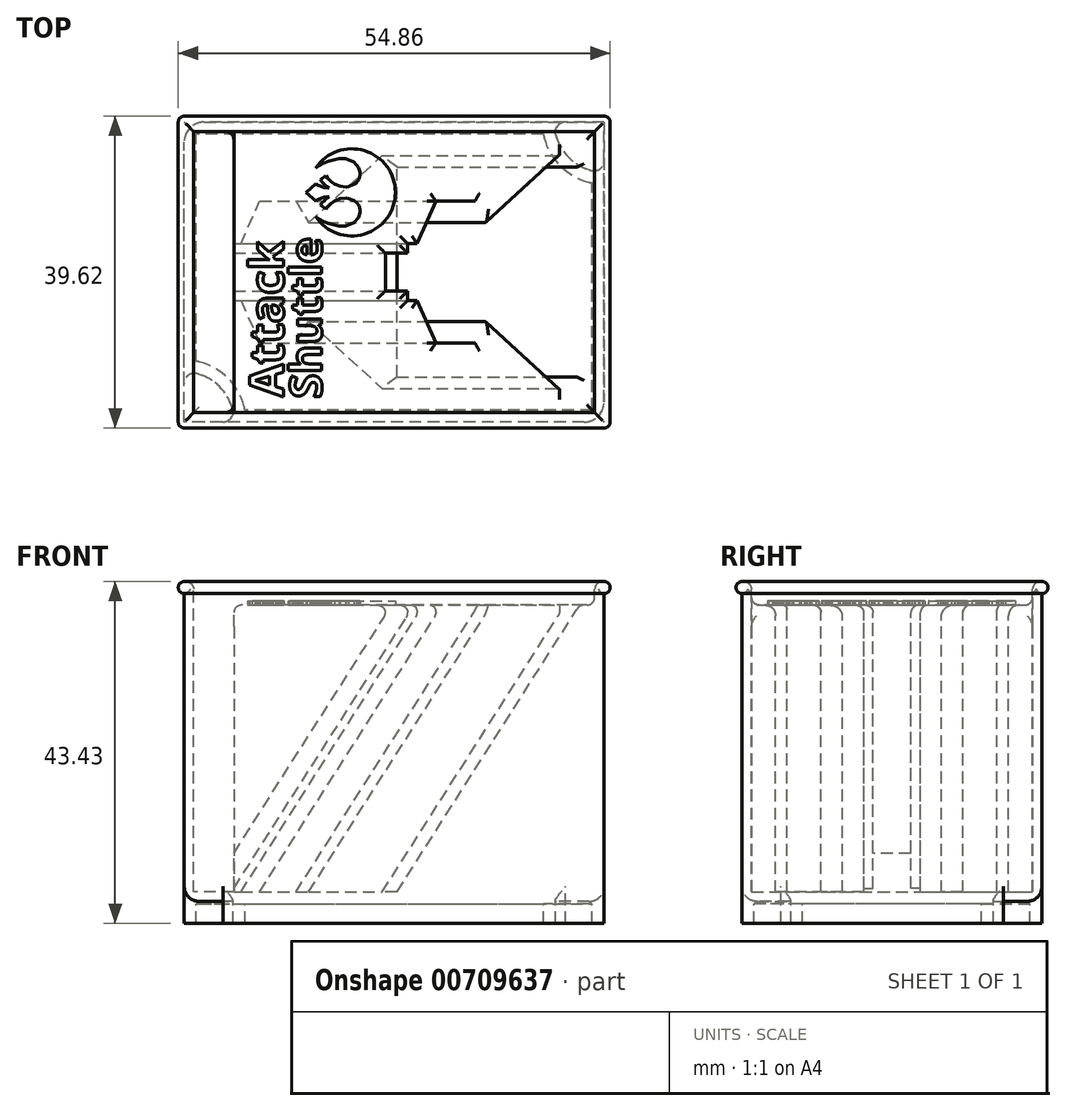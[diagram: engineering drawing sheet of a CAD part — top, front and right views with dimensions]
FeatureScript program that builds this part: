
annotation { "Feature Type Name" : "Feature", "Feature Type Description" : "" }
export const myFeature = defineFeature(function(context is Context, id is Id, definition is map)
    precondition{}
    {
        {
            var Q0;
            Q0=qCreatedBy(makeId("Front.planeOp"),FACE);
            var sketch = newSketch(context, id + "F0", { "sketchPlane" : qUnion([Q0])});
            skLineSegment(sketch, "E0.bottom", {"start": v(26.67, -20.32) * mm, "end": v(-26.67, -20.32) * mm});
            skLineSegment(sketch, "E0.top", {"start": v(26.67, 20.32) * mm, "end": v(-26.67, 20.32) * mm});
            skLineSegment(sketch, "E0.left", {"start": v(26.67, -20.32) * mm, "end": v(26.67, 20.32) * mm});
            skLineSegment(sketch, "E0.right", {"start": v(-26.67, -20.32) * mm, "end": v(-26.67, 20.32) * mm});
            skPoint(sketch, "E0.middle", {"position": v(0, 0) * mm});
            skSolve(sketch);
        }
        {
            var Q0;
            Q0=makeQuery(id+"F0.imprint","IMPRINT",FACE,{"disambiguationData":[TD([[makeQuery(id+"F0.imprint","IMPRINT",EDGE,{"derivedFrom":sQuery(id+"F0.wireOp",EDGE,"E0.bottom")}),-1.0]])]});
            extrude(context, id + "F1", {"entities" : qUnion([Q0]), "depth" : 38.1 * mm, "symmetric" : true});
        }
        {
            var Q0;
            Q0=makeQuery(id+"F1.opExtrude","SWEPT_FACE",FACE,{"disambiguationData":[OSD([sQuery(id+"F0.wireOp",EDGE,"E0.top")])]});
            shell(context, id + "F2", {"entities" : qUnion([Q0]), "thickness" : 1.2 * mm});
        }
        {
            var Q0;
            Q0=makeQuery(id+"F1.opExtrude","CAP_FACE",FACE,{"disambiguationData":[OSD([sQuery(id+"F0.wireOp",EDGE,"E0.bottom"),sQuery(id+"F0.wireOp",EDGE,"E0.top"),sQuery(id+"F0.wireOp",EDGE,"E0.left"),sQuery(id+"F0.wireOp",EDGE,"E0.right")])],"isStart":false});
            var sketch = newSketch(context, id + "F3", { "sketchPlane" : qUnion([Q0])});
            skArc(sketch, "E1", {"start": v(-26.67, 20.32) * mm, "mid": v(-27.43, 19.56) * mm, "end": v(-26.67, 18.8) * mm});
            skSolve(sketch);
        }
        {
            var Q0;
            {var subQ0=sQuery(id+"F3.wireOp",EDGE,"E1");Q0=makeQuery(id+"F3.imprint","IMPRINT",FACE,{"disambiguationData":[TD([[makeQuery(id+"F3.imprint","IMPRINT",EDGE,{"derivedFrom":subQ0}),1.0]])]});}
            var Q1;
            Q1=makeQuery(id+"F1.opExtrude","SWEPT_EDGE",EDGE,{"disambiguationData":[OSD([sQuery(id+"F0.wireOp",EDGE,"E0.top"),sQuery(id+"F0.wireOp",EDGE,"E0.right")])]});
            var Q2;
            Q2=makeQuery(id+"F1.opExtrude","CAP_EDGE",EDGE,{"disambiguationData":[OSD([sQuery(id+"F0.wireOp",EDGE,"E0.top")])],"isStart":true});
            var Q3;
            Q3=makeQuery(id+"F1.opExtrude","SWEPT_EDGE",EDGE,{"disambiguationData":[OSD([sQuery(id+"F0.wireOp",EDGE,"E0.top"),sQuery(id+"F0.wireOp",EDGE,"E0.left")])]});
            var Q4;
            Q4=makeQuery(id+"F1.opExtrude","CAP_EDGE",EDGE,{"disambiguationData":[OSD([sQuery(id+"F0.wireOp",EDGE,"E0.top")])],"isStart":false});
            sweep(context, id + "F4", {"operationType" : NewBodyOperationType.ADD, "profiles" : qUnion([Q0]), "path" : qUnion([Q1, Q2, Q3, Q4])});
        }
        {
            var Q0;
            Q0=makeQuery(id+"F1.opExtrude","SWEPT_FACE",FACE,{"disambiguationData":[OSD([sQuery(id+"F0.wireOp",EDGE,"E0.bottom")])]});
            var sketch = newSketch(context, id + "F5", { "sketchPlane" : qUnion([Q0])});
            skLineSegment(sketch, "E2.bottom", {"start": v(26.67, 19.05) * mm, "end": v(21.75, 19.05) * mm});
            skLineSegment(sketch, "E2.left", {"start": v(26.67, 19.05) * mm, "end": v(26.67, 14.13) * mm});
            skPoint(sketch, "E3.newPointA", {"position": v(20.32, 19.05) * mm});
            skArc(sketch, "E4", {"start": v(20.52, 17.46) * mm, "mid": v(22.18, 14.56) * mm, "end": v(25.08, 12.9) * mm});
            skArc(sketch, "E5.filletArc", {"start": v(21.75, 19.05) * mm, "mid": v(20.75, 18.56) * mm, "end": v(20.52, 17.46) * mm});
            skPoint(sketch, "E6.visualSharp", {"position": v(26.67, 12.7) * mm});
            skArc(sketch, "E6.filletArc", {"start": v(25.08, 12.9) * mm, "mid": v(26.18, 13.13) * mm, "end": v(26.67, 14.13) * mm});
            skArc(sketch, "E7.MirrorCS", {"start": v(-21.75, 19.05) * mm, "mid": v(-20.75, 18.56) * mm, "end": v(-20.52, 17.46) * mm});
            skArc(sketch, "E8.MirrorCS", {"start": v(-20.52, 17.46) * mm, "mid": v(-22.18, 14.56) * mm, "end": v(-25.08, 12.9) * mm});
            skArc(sketch, "E9.MirrorCS", {"start": v(-25.08, 12.9) * mm, "mid": v(-26.18, 13.13) * mm, "end": v(-26.67, 14.13) * mm});
            skLineSegment(sketch, "E10.MirrorCS", {"start": v(-26.67, 19.05) * mm, "end": v(-26.67, 14.13) * mm});
            skLineSegment(sketch, "E11.MirrorCS", {"start": v(-26.67, 19.05) * mm, "end": v(-21.75, 19.05) * mm});
            skArc(sketch, "E12.MirrorCS", {"start": v(-20.52, -17.46) * mm, "mid": v(-22.18, -14.56) * mm, "end": v(-25.08, -12.9) * mm});
            skArc(sketch, "E13.MirrorCS", {"start": v(-21.75, -19.05) * mm, "mid": v(-20.75, -18.56) * mm, "end": v(-20.52, -17.46) * mm});
            skLineSegment(sketch, "E14.MirrorCS", {"start": v(-26.67, -19.05) * mm, "end": v(-21.75, -19.05) * mm});
            skLineSegment(sketch, "E15.MirrorCS", {"start": v(-26.67, -19.05) * mm, "end": v(-26.67, -14.13) * mm});
            skArc(sketch, "E16.MirrorCS", {"start": v(-25.08, -12.9) * mm, "mid": v(-26.18, -13.13) * mm, "end": v(-26.67, -14.13) * mm});
            skArc(sketch, "E17.MirrorCS", {"start": v(21.75, -19.05) * mm, "mid": v(20.75, -18.56) * mm, "end": v(20.52, -17.46) * mm});
            skArc(sketch, "E18.MirrorCS", {"start": v(20.52, -17.46) * mm, "mid": v(22.18, -14.56) * mm, "end": v(25.08, -12.9) * mm});
            skArc(sketch, "E19.MirrorCS", {"start": v(25.08, -12.9) * mm, "mid": v(26.18, -13.13) * mm, "end": v(26.67, -14.13) * mm});
            skLineSegment(sketch, "E20.MirrorCS", {"start": v(26.67, -19.05) * mm, "end": v(26.67, -14.13) * mm});
            skLineSegment(sketch, "E21.MirrorCS", {"start": v(26.67, -19.05) * mm, "end": v(21.75, -19.05) * mm});
            skSolve(sketch);
        }
        {
            var Q0;
            Q0=makeQuery(id+"F5.imprint","IMPRINT",FACE,{"disambiguationData":[TD([[makeQuery(id+"F5.imprint","IMPRINT",EDGE,{"derivedFrom":sQuery(id+"F5.wireOp",EDGE,"E2.bottom")}),1.0]])]});
            var Q1;
            Q1=makeQuery(id+"F5.imprint","IMPRINT",FACE,{"disambiguationData":[TD([[makeQuery(id+"F5.imprint","IMPRINT",EDGE,{"derivedFrom":sQuery(id+"F5.wireOp",EDGE,"E8.MirrorCS")}),-1.0]])]});
            var Q2;
            Q2=makeQuery(id+"F5.imprint","IMPRINT",FACE,{"disambiguationData":[TD([[makeQuery(id+"F5.imprint","IMPRINT",EDGE,{"derivedFrom":sQuery(id+"F5.wireOp",EDGE,"E12.MirrorCS")}),1.0]])]});
            var Q3;
            Q3=makeQuery(id+"F5.imprint","IMPRINT",FACE,{"disambiguationData":[TD([[makeQuery(id+"F5.imprint","IMPRINT",EDGE,{"derivedFrom":sQuery(id+"F5.wireOp",EDGE,"E17.MirrorCS")}),-1.0]])]});
            extrude(context, id + "F6", {"entities" : qUnion([Q0, Q1, Q2, Q3]), "operationType" : NewBodyOperationType.ADD, "depth" : 2.8 * mm});
        }
        {
            var Q0;
            Q0=makeQuery(id+"F6.opExtrude","CAP_FACE",FACE,{"disambiguationData":[OSD([sQuery(id+"F5.wireOp",EDGE,"E2.bottom"),sQuery(id+"F5.wireOp",EDGE,"E2.left"),sQuery(id+"F5.wireOp",EDGE,"E4"),sQuery(id+"F5.wireOp",EDGE,"E5.filletArc"),sQuery(id+"F5.wireOp",EDGE,"E6.filletArc")])],"isStart":false});
            var Q1;
            Q1=makeQuery(id+"F6.opExtrude","CAP_FACE",FACE,{"disambiguationData":[OSD([sQuery(id+"F5.wireOp",EDGE,"E8.MirrorCS"),sQuery(id+"F5.wireOp",EDGE,"E9.MirrorCS"),sQuery(id+"F5.wireOp",EDGE,"E10.MirrorCS"),sQuery(id+"F5.wireOp",EDGE,"E7.MirrorCS"),sQuery(id+"F5.wireOp",EDGE,"E11.MirrorCS")])],"isStart":false});
            var Q2;
            Q2=makeQuery(id+"F6.opExtrude","CAP_FACE",FACE,{"disambiguationData":[OSD([sQuery(id+"F5.wireOp",EDGE,"E12.MirrorCS"),sQuery(id+"F5.wireOp",EDGE,"E13.MirrorCS"),sQuery(id+"F5.wireOp",EDGE,"E14.MirrorCS"),sQuery(id+"F5.wireOp",EDGE,"E15.MirrorCS"),sQuery(id+"F5.wireOp",EDGE,"E16.MirrorCS")])],"isStart":false});
            var Q3;
            Q3=makeQuery(id+"F6.opExtrude","CAP_FACE",FACE,{"disambiguationData":[OSD([sQuery(id+"F5.wireOp",EDGE,"E17.MirrorCS"),sQuery(id+"F5.wireOp",EDGE,"E18.MirrorCS"),sQuery(id+"F5.wireOp",EDGE,"E19.MirrorCS"),sQuery(id+"F5.wireOp",EDGE,"E20.MirrorCS"),sQuery(id+"F5.wireOp",EDGE,"E21.MirrorCS")])],"isStart":false});
            shell(context, id + "F7", {"entities" : qUnion([Q0, Q1, Q2, Q3]), "thickness" : 1.52 * mm});
        }
        {
            var Q0;
            Q0=makeQuery(id+"F1.opExtrude","SWEPT_EDGE",EDGE,{"disambiguationData":[OSD([sQuery(id+"F0.wireOp",EDGE,"E0.bottom"),sQuery(id+"F0.wireOp",EDGE,"E0.right")])]});
            var Q1;
            Q1=makeQuery(id+"F1.opExtrude","CAP_EDGE",EDGE,{"disambiguationData":[OSD([sQuery(id+"F0.wireOp",EDGE,"E0.bottom")])],"isStart":false});
            var Q2;
            Q2=makeQuery(id+"F1.opExtrude","SWEPT_EDGE",EDGE,{"disambiguationData":[OSD([sQuery(id+"F0.wireOp",EDGE,"E0.bottom"),sQuery(id+"F0.wireOp",EDGE,"E0.left")])]});
            var Q3;
            Q3=makeQuery(id+"F1.opExtrude","CAP_EDGE",EDGE,{"disambiguationData":[OSD([sQuery(id+"F0.wireOp",EDGE,"E0.bottom")])],"isStart":true});
            fillet(context, id + "F8", {"entities" : qUnion([Q0, Q1, Q2, Q3]), "radius" : 1.9 * mm, "tangentPropagation" : true, "allowEdgeOverflow" : false});
        }
        {
            var Q0;
            Q0=makeQuery(id+"F4.opSweep","MID_CAP_EDGE",EDGE,{"disambiguationData":[OSD([sQuery(id+"F0.wireOp",EDGE,"E0.top"),sQuery(id+"F0.wireOp",EDGE,"E0.left"),sQuery(id+"F3.wireOp",EDGE,"E1")])],"capPos":3.0});
            var Q1;
            Q1=makeQuery(id+"F4.opSweep","MID_CAP_EDGE",EDGE,{"disambiguationData":[OSD([sQuery(id+"F0.wireOp",EDGE,"E0.top"),sQuery(id+"F0.wireOp",EDGE,"E0.left"),sQuery(id+"F3.wireOp",EDGE,"E1")])],"capPos":2.0});
            var Q2;
            Q2=makeQuery(id+"F4.opSweep","MID_CAP_EDGE",EDGE,{"disambiguationData":[OSD([sQuery(id+"F0.wireOp",EDGE,"E0.top"),sQuery(id+"F0.wireOp",EDGE,"E0.right"),sQuery(id+"F3.wireOp",EDGE,"E1")])],"capPos":1.0});
            var Q3;
            Q3=makeQuery(id+"F4.opSweep","CAP_EDGE",EDGE,{"disambiguationData":[OSD([sQuery(id+"F0.wireOp",EDGE,"E0.top"),sQuery(id+"F0.wireOp",EDGE,"E0.right"),sQuery(id+"F3.wireOp",EDGE,"E1")])],"isStart":true});
            fillet(context, id + "F9", {"entities" : qUnion([Q0, Q1, Q2, Q3]), "radius" : 0.76 * mm, "tangentPropagation" : true, "allowEdgeOverflow" : false});
        }
        {
            var Q0;
            Q0=makeQuery(id+"F6.boolean.opBoolean","MERGE",EDGE,{"derivedFrom":[makeQuery(id+"F1.opExtrude","CAP_EDGE",EDGE,{"disambiguationData":[OSD([sQuery(id+"F0.wireOp",EDGE,"E0.left")])],"isStart":false}),makeQuery(id+"F6.opExtrude","SWEPT_EDGE",EDGE,{"disambiguationData":[OSD([sQuery(id+"F5.wireOp",EDGE,"E2.bottom"),sQuery(id+"F5.wireOp",EDGE,"E2.left")])]})]});
            var Q1;
            Q1=makeQuery(id+"F6.boolean.opBoolean","MERGE",EDGE,{"derivedFrom":[makeQuery(id+"F1.opExtrude","CAP_EDGE",EDGE,{"disambiguationData":[OSD([sQuery(id+"F0.wireOp",EDGE,"E0.left")])],"isStart":true}),makeQuery(id+"F6.opExtrude","SWEPT_EDGE",EDGE,{"disambiguationData":[OSD([sQuery(id+"F5.wireOp",EDGE,"E20.MirrorCS"),sQuery(id+"F5.wireOp",EDGE,"E21.MirrorCS")])]})]});
            var Q2;
            Q2=makeQuery(id+"F6.boolean.opBoolean","MERGE",EDGE,{"derivedFrom":[makeQuery(id+"F1.opExtrude","CAP_EDGE",EDGE,{"disambiguationData":[OSD([sQuery(id+"F0.wireOp",EDGE,"E0.right")])],"isStart":false}),makeQuery(id+"F6.opExtrude","SWEPT_EDGE",EDGE,{"disambiguationData":[OSD([sQuery(id+"F5.wireOp",EDGE,"E10.MirrorCS"),sQuery(id+"F5.wireOp",EDGE,"E11.MirrorCS")])]})]});
            var Q3;
            Q3=makeQuery(id+"F6.boolean.opBoolean","MERGE",EDGE,{"derivedFrom":[makeQuery(id+"F1.opExtrude","CAP_EDGE",EDGE,{"disambiguationData":[OSD([sQuery(id+"F0.wireOp",EDGE,"E0.right")])],"isStart":true}),makeQuery(id+"F6.opExtrude","SWEPT_EDGE",EDGE,{"disambiguationData":[OSD([sQuery(id+"F5.wireOp",EDGE,"E14.MirrorCS"),sQuery(id+"F5.wireOp",EDGE,"E15.MirrorCS")])]})]});
            fillet(context, id + "F10", {"entities" : qUnion([Q0, Q1, Q2, Q3]), "radius" : 2.54 * mm, "tangentPropagation" : true, "allowEdgeOverflow" : false});
        }
        {
            var Q0;
            Q0=makeQuery(id+"F2.opShell","OFFSET_EDGE",EDGE,{"disambiguationData":[OSD([sQuery(id+"F0.wireOp",EDGE,"E0.top"),sQuery(id+"F0.wireOp",EDGE,"E0.left")])]});
            cPlane(context, id + "F11", {"entities" : qUnion([Q0]), "cplaneType" : CPlaneType.LINE_ANGLE, "offset" : 25 * mm, "angle" : 32.5 * degree, "width" : 150 * mm, "height" : 150 * mm});
        }
        {
            var Q0;
            Q0=qCreatedBy(id+"F11.planeOp",FACE);
            var sketch = newSketch(context, id + "F12", { "sketchPlane" : qUnion([Q0])});
            skLineSegment(sketch, "E22", {"start": v(58.48, 35.77) * mm, "end": v(58.48, -3.33) * mm});
            skLineSegment(sketch, "E23", {"start": v(58.48, -3.33) * mm, "end": v(83.38, -3.33) * mm});
            skLineSegment(sketch, "E24", {"start": v(83.38, -3.33) * mm, "end": v(58.48, 35.77) * mm});
            skLineSegment(sketch, "E25", {"start": v(10.79, -61.22) * mm, "end": v(10.79, -63.22) * mm});
            skLineSegment(sketch, "E26", {"start": v(10.79, -63.22) * mm, "end": v(16.55, -63.22) * mm});
            skLineSegment(sketch, "E27", {"start": v(7.55, -61.22) * mm, "end": v(5.55, -57.22) * mm});
            skLineSegment(sketch, "E28", {"start": v(2.55, -57.22) * mm, "end": v(5.55, -57.22) * mm});
            skLineSegment(sketch, "E29", {"start": v(16.55, -63.22) * mm, "end": v(16.55, -66.22) * mm});
            skLineSegment(sketch, "E30", {"start": v(7.55, -61.22) * mm, "end": v(7.55, -60.22) * mm});
            skPoint(sketch, "E31", {"position": v(15.68, -51.42) * mm});
            skPoint(sketch, "E32", {"position": v(17.27, -52.89) * mm});
            skLineSegment(sketch, "E33", {"start": v(10.79, -61.22) * mm, "end": v(17.27, -52.89) * mm});
            skLineSegment(sketch, "E34", {"start": v(7.55, -60.22) * mm, "end": v(15.68, -51.42) * mm});
            skLineSegment(sketch, "E35", {"start": v(17.27, -52.89) * mm, "end": v(15.68, -51.42) * mm});
            skLineSegment(sketch, "E36", {"start": v(-2.85, -66.22) * mm, "end": v(-2.85, -63.82) * mm});
            skLineSegment(sketch, "E37", {"start": v(-2.85, -63.82) * mm, "end": v(-0.45, -63.82) * mm});
            skLineSegment(sketch, "E38", {"start": v(-0.45, -63.82) * mm, "end": v(-0.45, -62.62) * mm});
            skLineSegment(sketch, "E39", {"start": v(-0.45, -62.62) * mm, "end": v(0.55, -62.62) * mm});
            skLineSegment(sketch, "E40", {"start": v(0.55, -62.62) * mm, "end": v(2.55, -57.22) * mm});
            skLineSegment(sketch, "E41.MirrorCS", {"start": v(17.27, -79.55) * mm, "end": v(15.68, -81.01) * mm});
            skLineSegment(sketch, "E42.MirrorCS", {"start": v(-0.45, -69.82) * mm, "end": v(0.55, -69.82) * mm});
            skLineSegment(sketch, "E43.MirrorCS", {"start": v(-0.45, -68.62) * mm, "end": v(-0.45, -69.82) * mm});
            skLineSegment(sketch, "E44.MirrorCS", {"start": v(7.55, -71.22) * mm, "end": v(7.55, -72.22) * mm});
            skLineSegment(sketch, "E45.MirrorCS", {"start": v(10.79, -71.22) * mm, "end": v(10.79, -69.22) * mm});
            skLineSegment(sketch, "E46.MirrorCS", {"start": v(-2.85, -68.62) * mm, "end": v(-0.45, -68.62) * mm});
            skLineSegment(sketch, "E47.MirrorCS", {"start": v(10.79, -69.22) * mm, "end": v(16.55, -69.22) * mm});
            skLineSegment(sketch, "E48.MirrorCS", {"start": v(7.55, -72.22) * mm, "end": v(15.68, -81.01) * mm});
            skLineSegment(sketch, "E49.MirrorCS", {"start": v(16.55, -69.22) * mm, "end": v(16.55, -66.22) * mm});
            skLineSegment(sketch, "E50.MirrorCS", {"start": v(0.55, -69.82) * mm, "end": v(2.55, -75.22) * mm});
            skLineSegment(sketch, "E51.MirrorCS", {"start": v(10.79, -71.22) * mm, "end": v(17.27, -79.55) * mm});
            skLineSegment(sketch, "E52.MirrorCS", {"start": v(2.55, -75.22) * mm, "end": v(5.55, -75.22) * mm});
            skLineSegment(sketch, "E53.MirrorCS", {"start": v(7.55, -71.22) * mm, "end": v(5.55, -75.22) * mm});
            skLineSegment(sketch, "E54.MirrorCS", {"start": v(-2.85, -66.22) * mm, "end": v(-2.85, -68.62) * mm});
            skPoint(sketch, "E55.MirrorP", {"position": v(15.68, -81.01) * mm});
            skPoint(sketch, "E56.MirrorP", {"position": v(17.27, -79.55) * mm});
            skLineSegment(sketch, "E57", {"start": v(17.27, -81.01) * mm, "end": v(17.27, -51.42) * mm, "construction": true});
            skLineSegment(sketch, "E58", {"start": v(17.27, -51.42) * mm, "end": v(-2.85, -51.42) * mm, "construction": true});
            skLineSegment(sketch, "E59", {"start": v(17.27, -81.01) * mm, "end": v(-2.85, -81.01) * mm, "construction": true});
            skLineSegment(sketch, "E60", {"start": v(16.55, -66.22) * mm, "end": v(17.27, -66.22) * mm, "construction": true});
            skLineSegment(sketch, "E61", {"start": v(4.08, 5) * mm, "end": v(4.08, 3) * mm});
            skLineSegment(sketch, "E62", {"start": v(4.08, 3) * mm, "end": v(9.84, 3) * mm});
            skLineSegment(sketch, "E63", {"start": v(9.84, 3) * mm, "end": v(9.84, 0) * mm});
            skPoint(sketch, "E64", {"position": v(8.98, 14.8) * mm});
            skPoint(sketch, "E65", {"position": v(10.57, 13.33) * mm});
            skLineSegment(sketch, "E66", {"start": v(4.08, 5) * mm, "end": v(10.57, 13.33) * mm});
            skLineSegment(sketch, "E67", {"start": v(10.57, 13.33) * mm, "end": v(8.98, 14.8) * mm});
            skLineSegment(sketch, "E68", {"start": v(-9.56, 0) * mm, "end": v(-9.56, 2.4) * mm});
            skLineSegment(sketch, "E69", {"start": v(-9.56, 2.4) * mm, "end": v(-7.16, 2.4) * mm});
            skLineSegment(sketch, "E70", {"start": v(-7.16, 2.4) * mm, "end": v(-7.16, 3.6) * mm});
            skLineSegment(sketch, "E71", {"start": v(-7.16, 3.6) * mm, "end": v(-6.16, 3.6) * mm});
            skLineSegment(sketch, "E72", {"start": v(-6.16, 3.6) * mm, "end": v(-4.16, 9) * mm});
            skLineSegment(sketch, "E73.MirrorCS", {"start": v(10.57, -13.33) * mm, "end": v(8.98, -14.8) * mm});
            skLineSegment(sketch, "E74.MirrorCS", {"start": v(-7.16, -3.6) * mm, "end": v(-6.16, -3.6) * mm});
            skLineSegment(sketch, "E75.MirrorCS", {"start": v(-7.16, -2.4) * mm, "end": v(-7.16, -3.6) * mm});
            skLineSegment(sketch, "E76.MirrorCS", {"start": v(4.08, -5) * mm, "end": v(4.08, -3) * mm});
            skLineSegment(sketch, "E77.MirrorCS", {"start": v(-9.56, -2.4) * mm, "end": v(-7.16, -2.4) * mm});
            skLineSegment(sketch, "E78.MirrorCS", {"start": v(4.08, -3) * mm, "end": v(9.84, -3) * mm});
            skLineSegment(sketch, "E79.MirrorCS", {"start": v(1.1, -6.28) * mm, "end": v(8.98, -14.8) * mm});
            skLineSegment(sketch, "E80.MirrorCS", {"start": v(9.84, -3) * mm, "end": v(9.84, 0) * mm});
            skLineSegment(sketch, "E81.MirrorCS", {"start": v(-6.16, -3.6) * mm, "end": v(-4.16, -9) * mm});
            skLineSegment(sketch, "E82.MirrorCS", {"start": v(4.08, -5) * mm, "end": v(10.57, -13.33) * mm});
            skLineSegment(sketch, "E83.MirrorCS", {"start": v(-9.56, 0) * mm, "end": v(-9.56, -2.4) * mm});
            skPoint(sketch, "E84.MirrorP", {"position": v(8.98, -14.8) * mm});
            skPoint(sketch, "E85.MirrorP", {"position": v(10.57, -13.33) * mm});
            skLineSegment(sketch, "E86", {"start": v(-4.16, -9) * mm, "end": v(-0.26, -9) * mm});
            skLineSegment(sketch, "E87", {"start": v(-0.26, -9) * mm, "end": v(1.1, -6.28) * mm});
            skLineSegment(sketch, "E88.MirrorCS", {"start": v(1.1, 6.28) * mm, "end": v(8.98, 14.8) * mm});
            skLineSegment(sketch, "E89.MirrorCS", {"start": v(-0.26, 9) * mm, "end": v(1.1, 6.28) * mm});
            skLineSegment(sketch, "E90.MirrorCS", {"start": v(-4.16, 9) * mm, "end": v(-0.26, 9) * mm});
            skLineSegment(sketch, "E91", {"start": v(10.57, -14.8) * mm, "end": v(10.57, 14.8) * mm, "construction": true});
            skLineSegment(sketch, "E92.0", {"start": v(10.57, -17.85) * mm, "end": v(10.57, 17.85) * mm});
            skSolve(sketch);
        }
        {
            var Q0;
            Q0=makeQuery(id+"F2.opShell","OFFSET_FACE",FACE,{"disambiguationData":[OSD([sQuery(id+"F0.wireOp",EDGE,"E0.bottom")])]});
            var sketch = newSketch(context, id + "F13", { "sketchPlane" : qUnion([Q0])});
            skLineSegment(sketch, "E93.bottom", {"start": v(-25.47, -17.85) * mm, "end": v(-25.47, 17.85) * mm});
            skLineSegment(sketch, "E93.top", {"start": v(-20.37, -17.85) * mm, "end": v(-20.37, 17.85) * mm});
            skPoint(sketch, "E93.middle", {"position": v(-22.6, 0) * mm});
            skLineSegment(sketch, "E94.0", {"start": v(25.47, 17.85) * mm, "end": v(-20.37, 17.85) * mm});
            skLineSegment(sketch, "E94.1", {"start": v(25.47, -17.85) * mm, "end": v(-20.37, -17.85) * mm});
            skLineSegment(sketch, "E94.2", {"start": v(25.15, -17.53) * mm, "end": v(25.15, 17.53) * mm});
            skPoint(sketch, "E95.orphan", {"position": v(-25.47, -17.85) * mm});
            skPoint(sketch, "E96.orphan", {"position": v(-25.47, 17.85) * mm});
            skSolve(sketch);
        }
        {
            var Q0;
            {var subQ0=sQuery(id+"F13.wireOp",EDGE,"E93.bottom");var subQ1=sQuery(id+"F0.wireOp",EDGE,"E0.bottom");var subQ2=makeQuery(id+"F2.opShell","OFFSET_EDGE",EDGE,{"disambiguationData":[OSD([subQ1]),TDD([makeQuery(id+"F1.opExtrude","CAP_EDGE",EDGE,{"disambiguationData":[OSD([subQ1])],"isStart":true})])]});var subQ3=makeQuery(id+"F13.imprint","INTERSECT",VERTEX,{"derivedFrom":[subQ2,subQ0]});Q0=makeQuery(id+"F13.imprint","IMPRINT",FACE,{"disambiguationData":[TD([[makeQuery(id+"F13.imprint","IMPRINT",EDGE,{"disambiguationData":[TD([[subQ3,1.0]])],"derivedFrom":subQ0}),-1.0]])]});}
            var Q1;
            {var subQ4=sQuery(id+"F13.wireOp",EDGE,"E93.left");Q1=makeQuery(id+"F13.imprint","IMPRINT",FACE,{"disambiguationData":[TD([[makeQuery(id+"F13.imprint","IMPRINT",EDGE,{"derivedFrom":subQ4}),1.0]])]});}
            var Q2;
            {var subQ4=sQuery(id+"F13.wireOp",EDGE,"E93.right");Q2=makeQuery(id+"F13.imprint","IMPRINT",FACE,{"disambiguationData":[TD([[makeQuery(id+"F13.imprint","IMPRINT",EDGE,{"derivedFrom":subQ4}),-1.0]])]});}
            var Q3;
            {var subQ0=sQuery(id+"F0.wireOp",EDGE,"E0.right");var subQ1=sQuery(id+"F0.wireOp",EDGE,"E0.top");Q3=makeQuery(id+"F2.opShell","OFFSET_VERTEX",VERTEX,{"disambiguationData":[OSD([subQ1,subQ0]),TDD([makeQuery(id+"F1.opExtrude","CAP_VERTEX",VERTEX,{"disambiguationData":[OSD([subQ1,subQ0])],"isStart":true})])]});}
            extrude(context, id + "F14", {"entities" : qUnion([Q0, Q1, Q2]), "operationType" : NewBodyOperationType.REMOVE, "endBound" : BoundingType.UP_TO_VERTEX, "depth" : 25 * mm, "endBoundEntityVertex" : qUnion([Q3]), "offsetDistance" : 25 * mm});
        }
        {
            var Q0;
            {var subQ0=sQuery(id+"F13.wireOp",EDGE,"E94.0");Q0=makeQuery(id+"F13.imprint","IMPRINT",FACE,{"disambiguationData":[TD([[makeQuery(id+"F13.imprint","IMPRINT",EDGE,{"derivedFrom":subQ0}),1.0]])]});}
            extrude(context, id + "F15", {"entities" : qUnion([Q0]), "operationType" : NewBodyOperationType.ADD, "depth" : 36.44 * mm, "offsetDistance" : 25 * mm});
        }
        {
            var Q0;
            Q0 = qSketchRegion(id + "F12", true);
            var Q1;
            Q1=makeQuery(id+"F14.boolean.opBoolean","MERGE",FACE,{"derivedFrom":[makeQuery(id+"F2.opShell","OFFSET_FACE",FACE,{"disambiguationData":[OSD([sQuery(id+"F0.wireOp",EDGE,"E0.bottom")])]})],"fromTools":[makeQuery(id+"F14.opExtrude","CAP_FACE",FACE,{"disambiguationData":[OSD([sQuery(id+"F13.wireOp",EDGE,"E93.bottom"),sQuery(id+"F13.wireOp",EDGE,"E93.top"),sQuery(id+"F13.wireOp",EDGE,"E93.left"),sQuery(id+"F13.wireOp",EDGE,"E93.right")])],"isStart":true})]});
            extrude(context, id + "F16", {"entities" : qUnion([Q0]), "operationType" : NewBodyOperationType.REMOVE, "endBound" : BoundingType.UP_TO_SURFACE, "oppositeDirection" : true, "depth" : 25 * mm, "endBoundEntityFace" : qUnion([Q1]), "offsetDistance" : 25 * mm});
        }
        {
            var Q0;
            Q0=makeQuery(id+"F15.opExtrude","CAP_FACE",FACE,{"disambiguationData":[OSD([sQuery(id+"F0.wireOp",EDGE,"E0.bottom"),sQuery(id+"F0.wireOp",EDGE,"E0.left"),sQuery(id+"F0.wireOp",EDGE,"E0.right"),sQuery(id+"F13.wireOp",EDGE,"E93.bottom"),sQuery(id+"F13.wireOp",EDGE,"E93.top"),sQuery(id+"F13.wireOp",EDGE,"E93.left"),sQuery(id+"F13.wireOp",EDGE,"E93.right"),sQuery(id+"F13.wireOp",EDGE,"E94.0"),sQuery(id+"F13.wireOp",EDGE,"E94.1")])],"isStart":false});
            var Q1;
            Q1=makeQuery(id+"F2.opShell","OFFSET_EDGE",EDGE,{"disambiguationData":[OSD([sQuery(id+"F0.wireOp",EDGE,"E0.top"),sQuery(id+"F0.wireOp",EDGE,"E0.right")])]});
            var Q2;
            {var subQ0=sQuery(id+"F0.wireOp",EDGE,"E0.top");Q2=makeQuery(id+"F2.opShell","OFFSET_EDGE",EDGE,{"disambiguationData":[OSD([subQ0]),TDD([makeQuery(id+"F1.opExtrude","CAP_EDGE",EDGE,{"disambiguationData":[OSD([subQ0])],"isStart":true})])]});}
            var Q3;
            {var subQ0=sQuery(id+"F0.wireOp",EDGE,"E0.top");Q3=makeQuery(id+"F2.opShell","OFFSET_EDGE",EDGE,{"disambiguationData":[OSD([subQ0]),TDD([makeQuery(id+"F1.opExtrude","CAP_EDGE",EDGE,{"disambiguationData":[OSD([subQ0])],"isStart":false})])]});}
            var Q4;
            Q4=makeQuery(id+"F2.opShell","OFFSET_EDGE",EDGE,{"disambiguationData":[OSD([sQuery(id+"F0.wireOp",EDGE,"E0.top"),sQuery(id+"F0.wireOp",EDGE,"E0.left")])]});
            fillet(context, id + "F17", {"entities" : qUnion([Q0, Q1, Q2, Q3, Q4]), "radius" : 1 * mm, "tangentPropagation" : true, "allowEdgeOverflow" : false});
        }
        {
            var Q0;
            Q0=makeQuery(id+"F15.opExtrude","CAP_FACE",FACE,{"disambiguationData":[OSD([sQuery(id+"F0.wireOp",EDGE,"E0.bottom"),sQuery(id+"F0.wireOp",EDGE,"E0.left"),sQuery(id+"F13.wireOp",EDGE,"E93.top"),sQuery(id+"F13.wireOp",EDGE,"E94.0"),sQuery(id+"F13.wireOp",EDGE,"E94.1")])],"isStart":false});
            var sketch = newSketch(context, id + "F18", { "sketchPlane" : qUnion([Q0])});
            skLineSegment(sketch, "E97", {"start": v(-9.93, 11.22) * mm, "end": v(-11.18, 10.13) * mm});
            skLineSegment(sketch, "E98", {"start": v(-9.38, 11.72) * mm, "end": v(-8.67, 12.27) * mm});
            skLineSegment(sketch, "E99", {"start": v(-8.67, 12.27) * mm, "end": v(-8.44, 11.97) * mm});
            skLineSegment(sketch, "E100", {"start": v(-8.44, 11.97) * mm, "end": v(-7.99, 11.52) * mm});
            skLineSegment(sketch, "E101", {"start": v(-7.99, 11.52) * mm, "end": v(-7.58, 11.2) * mm});
            skLineSegment(sketch, "E102", {"start": v(-7.58, 11.2) * mm, "end": v(-6.88, 10.9) * mm});
            skLineSegment(sketch, "E103", {"start": v(-6.88, 10.9) * mm, "end": v(-6.13, 10.82) * mm});
            skLineSegment(sketch, "E104", {"start": v(-6.13, 10.82) * mm, "end": v(-5.76, 10.89) * mm});
            skLineSegment(sketch, "E105", {"start": v(-5.76, 10.89) * mm, "end": v(-5.07, 11.2) * mm});
            skLineSegment(sketch, "E106", {"start": v(-5.07, 11.2) * mm, "end": v(-4.75, 11.4) * mm});
            skLineSegment(sketch, "E107", {"start": v(-4.75, 11.4) * mm, "end": v(-4.46, 11.82) * mm});
            skLineSegment(sketch, "E108", {"start": v(-4.46, 11.82) * mm, "end": v(-4.31, 12.31) * mm});
            skLineSegment(sketch, "E109", {"start": v(-4.31, 12.31) * mm, "end": v(-4.31, 12.69) * mm});
            skLineSegment(sketch, "E110", {"start": v(-4.31, 12.69) * mm, "end": v(-4.5, 13.3) * mm});
            skLineSegment(sketch, "E111", {"start": v(-4.5, 13.3) * mm, "end": v(-5.12, 13.95) * mm});
            skLineSegment(sketch, "E112", {"start": v(-5.12, 13.95) * mm, "end": v(-6.15, 14.4) * mm});
            skLineSegment(sketch, "E113", {"start": v(-6.15, 14.4) * mm, "end": v(-7.03, 14.4) * mm});
            skLineSegment(sketch, "E114", {"start": v(-7.03, 14.4) * mm, "end": v(-8.28, 14.11) * mm});
            skLineSegment(sketch, "E115", {"start": v(-8.28, 14.11) * mm, "end": v(-8.99, 13.81) * mm});
            skLineSegment(sketch, "E116", {"start": v(-8.99, 13.81) * mm, "end": v(-9.54, 13.52) * mm});
            skLineSegment(sketch, "E117", {"start": v(-9.54, 13.52) * mm, "end": v(-9.96, 13.23) * mm});
            skLineSegment(sketch, "E118", {"start": v(-9.38, 11.72) * mm, "end": v(-9.22, 11.5) * mm});
            skLineSegment(sketch, "E119", {"start": v(-9.22, 11.5) * mm, "end": v(-8.86, 11.14) * mm});
            skLineSegment(sketch, "E120", {"start": v(-8.86, 11.14) * mm, "end": v(-8.6, 10.87) * mm});
            skLineSegment(sketch, "E121", {"start": v(-8.6, 10.87) * mm, "end": v(-8.28, 10.65) * mm});
            skLineSegment(sketch, "E122", {"start": v(-8.28, 10.65) * mm, "end": v(-8.91, 10.75) * mm});
            skLineSegment(sketch, "E123", {"start": v(-8.91, 10.75) * mm, "end": v(-9.38, 10.9) * mm});
            skLineSegment(sketch, "E124", {"start": v(-9.38, 10.9) * mm, "end": v(-9.72, 11.05) * mm});
            skLineSegment(sketch, "E125", {"start": v(-9.72, 11.05) * mm, "end": v(-9.93, 11.22) * mm});
            skPoint(sketch, "E126.start.orphan", {"position": v(-11.73, 10.13) * mm});
            skLineSegment(sketch, "E127.MirrorCS", {"start": v(-4.75, 8.85) * mm, "end": v(-4.46, 8.43) * mm});
            skLineSegment(sketch, "E128.MirrorCS", {"start": v(-8.99, 6.44) * mm, "end": v(-9.54, 6.73) * mm});
            skLineSegment(sketch, "E129.MirrorCS", {"start": v(-5.07, 9.06) * mm, "end": v(-4.75, 8.85) * mm});
            skLineSegment(sketch, "E130.MirrorCS", {"start": v(-6.15, 5.85) * mm, "end": v(-7.03, 5.85) * mm});
            skLineSegment(sketch, "E131.MirrorCS", {"start": v(-8.28, 9.6) * mm, "end": v(-8.91, 9.5) * mm});
            skLineSegment(sketch, "E132.MirrorCS", {"start": v(-8.44, 8.28) * mm, "end": v(-7.99, 8.73) * mm});
            skLineSegment(sketch, "E133.MirrorCS", {"start": v(-8.91, 9.5) * mm, "end": v(-9.38, 9.34) * mm});
            skLineSegment(sketch, "E134.MirrorCS", {"start": v(-9.38, 9.34) * mm, "end": v(-9.72, 9.2) * mm});
            skLineSegment(sketch, "E135.MirrorCS", {"start": v(-8.6, 9.38) * mm, "end": v(-8.28, 9.6) * mm});
            skLineSegment(sketch, "E136.MirrorCS", {"start": v(-4.31, 7.56) * mm, "end": v(-4.5, 6.95) * mm});
            skLineSegment(sketch, "E137.MirrorCS", {"start": v(-4.5, 6.95) * mm, "end": v(-5.12, 6.3) * mm});
            skLineSegment(sketch, "E138.MirrorCS", {"start": v(-9.54, 6.73) * mm, "end": v(-9.96, 7.02) * mm});
            skLineSegment(sketch, "E139.MirrorCS", {"start": v(-8.28, 6.14) * mm, "end": v(-8.99, 6.44) * mm});
            skLineSegment(sketch, "E140.MirrorCS", {"start": v(-9.22, 8.74) * mm, "end": v(-8.86, 9.1) * mm});
            skLineSegment(sketch, "E141.MirrorCS", {"start": v(-7.99, 8.73) * mm, "end": v(-7.58, 9.05) * mm});
            skLineSegment(sketch, "E142.MirrorCS", {"start": v(-4.46, 8.43) * mm, "end": v(-4.31, 7.94) * mm});
            skLineSegment(sketch, "E143.MirrorCS", {"start": v(-8.67, 7.98) * mm, "end": v(-8.44, 8.28) * mm});
            skLineSegment(sketch, "E144.MirrorCS", {"start": v(-9.38, 8.53) * mm, "end": v(-9.22, 8.74) * mm});
            skLineSegment(sketch, "E145.MirrorCS", {"start": v(-5.76, 9.36) * mm, "end": v(-5.07, 9.06) * mm});
            skLineSegment(sketch, "E146.MirrorCS", {"start": v(-9.38, 8.53) * mm, "end": v(-8.67, 7.98) * mm});
            skLineSegment(sketch, "E147.MirrorCS", {"start": v(-6.13, 9.43) * mm, "end": v(-5.76, 9.36) * mm});
            skLineSegment(sketch, "E148.MirrorCS", {"start": v(-7.58, 9.05) * mm, "end": v(-6.88, 9.35) * mm});
            skLineSegment(sketch, "E149.MirrorCS", {"start": v(-6.88, 9.35) * mm, "end": v(-6.13, 9.43) * mm});
            skLineSegment(sketch, "E150.MirrorCS", {"start": v(-8.86, 9.1) * mm, "end": v(-8.6, 9.38) * mm});
            skLineSegment(sketch, "E151.MirrorCS", {"start": v(-9.72, 9.2) * mm, "end": v(-9.93, 9.03) * mm});
            skLineSegment(sketch, "E152.MirrorCS", {"start": v(-4.31, 7.94) * mm, "end": v(-4.31, 7.56) * mm});
            skLineSegment(sketch, "E153.MirrorCS", {"start": v(-7.03, 5.85) * mm, "end": v(-8.28, 6.14) * mm});
            skLineSegment(sketch, "E154.MirrorCS", {"start": v(-9.93, 9.03) * mm, "end": v(-11.18, 10.13) * mm});
            skLineSegment(sketch, "E155.MirrorCS", {"start": v(-5.12, 6.3) * mm, "end": v(-6.15, 5.85) * mm});
            skCircle(sketch, "E156.MirrorC", {"center": v(-5.38, 10.13) * mm, "radius": 6.35 * mm});
            skArc(sketch, "E157", {"start": v(-9.96, 7.02) * mm, "mid": v(0.16, 10.13) * mm, "end": v(-9.96, 13.23) * mm});
            skText(sketch, "E158", { "text": "Attack", "fontName": "NotoSans-Bold.ttf"});
            skPoint(sketch, "E159.0", {"position": v(-19.37, -16.85) * mm});
            skLineSegment(sketch, "E160", {"start": v(-19.37, -15.85) * mm, "end": v(-18.37, -15.85) * mm, "construction": true});
            skText(sketch, "E161", { "text": "Shuttle", "fontName": "NotoSans-Bold.ttf"});
            skLineSegment(sketch, "E162", {"start": v(-9.2, -16.85) * mm, "end": v(-9.2, -16.05) * mm, "construction": true});
            skLineSegment(sketch, "E163", {"start": v(-13.25, -5.77) * mm, "end": v(-14.05, -5.77) * mm, "construction": true});
            const initialGuessF18  = {"E158": [-0.01405, -0.01585, 0, 1, 0.00432], "E161": [-0.0092, -0.01605, 0, 1, 0.00406]};
            skSetInitialGuess(sketch, initialGuessF18);
            skSolve(sketch);
        }
        {
            var Q0;
            Q0=makeQuery(id+"F18.imprint","IMPRINT",FACE,{"disambiguationData":[TD([[makeQuery(id+"F18.imprint","IMPRINT",EDGE,{"derivedFrom":sQuery(id+"F18.wireOp",EDGE,"E158.sketch_text.stroke-12")}),-1.0]])]});
            var Q1;
            Q1=makeQuery(id+"F18.imprint","IMPRINT",FACE,{"disambiguationData":[TD([[makeQuery(id+"F18.imprint","IMPRINT",EDGE,{"derivedFrom":sQuery(id+"F18.wireOp",EDGE,"E158.sketch_text.stroke-30")}),-1.0]])]});
            var Q2;
            Q2=makeQuery(id+"F18.imprint","IMPRINT",FACE,{"disambiguationData":[TD([[makeQuery(id+"F18.imprint","IMPRINT",EDGE,{"derivedFrom":sQuery(id+"F18.wireOp",EDGE,"E158.sketch_text.stroke-73")}),-1.0]])]});
            var Q3;
            Q3=makeQuery(id+"F18.imprint","IMPRINT",FACE,{"disambiguationData":[TD([[makeQuery(id+"F18.imprint","IMPRINT",EDGE,{"derivedFrom":sQuery(id+"F18.wireOp",EDGE,"E158.sketch_text.stroke-87")}),-1.0]])]});
            var Q4;
            Q4=makeQuery(id+"F18.imprint","IMPRINT",FACE,{"disambiguationData":[TD([[makeQuery(id+"F18.imprint","IMPRINT",EDGE,{"derivedFrom":sQuery(id+"F18.wireOp",EDGE,"E161.sketch_text.stroke-0")}),-1.0]])]});
            var Q5;
            Q5=makeQuery(id+"F18.imprint","IMPRINT",FACE,{"disambiguationData":[TD([[makeQuery(id+"F18.imprint","IMPRINT",EDGE,{"derivedFrom":sQuery(id+"F18.wireOp",EDGE,"E161.sketch_text.stroke-28")}),-1.0]])]});
            var Q6;
            Q6=makeQuery(id+"F18.imprint","IMPRINT",FACE,{"disambiguationData":[TD([[makeQuery(id+"F18.imprint","IMPRINT",EDGE,{"derivedFrom":sQuery(id+"F18.wireOp",EDGE,"E161.sketch_text.stroke-45")}),-1.0]])]});
            var Q7;
            Q7=makeQuery(id+"F18.imprint","IMPRINT",FACE,{"disambiguationData":[TD([[makeQuery(id+"F18.imprint","IMPRINT",EDGE,{"derivedFrom":sQuery(id+"F18.wireOp",EDGE,"E161.sketch_text.stroke-62")}),-1.0]])]});
            var Q8;
            Q8=makeQuery(id+"F18.imprint","IMPRINT",FACE,{"disambiguationData":[TD([[makeQuery(id+"F18.imprint","IMPRINT",EDGE,{"derivedFrom":sQuery(id+"F18.wireOp",EDGE,"E161.sketch_text.stroke-80")}),-1.0]])]});
            var Q9;
            Q9=makeQuery(id+"F18.imprint","IMPRINT",FACE,{"disambiguationData":[TD([[makeQuery(id+"F18.imprint","IMPRINT",EDGE,{"derivedFrom":sQuery(id+"F18.wireOp",EDGE,"E161.sketch_text.stroke-98")}),-1.0]])]});
            var Q10;
            Q10=makeQuery(id+"F18.imprint","IMPRINT",FACE,{"disambiguationData":[TD([[makeQuery(id+"F18.imprint","IMPRINT",EDGE,{"derivedFrom":sQuery(id+"F18.wireOp",EDGE,"E158.sketch_text.stroke-0")}),-1.0]])]});
            var Q11;
            Q11=makeQuery(id+"F18.imprint","IMPRINT",FACE,{"disambiguationData":[TD([[makeQuery(id+"F18.imprint","IMPRINT",EDGE,{"derivedFrom":sQuery(id+"F18.wireOp",EDGE,"E158.sketch_text.stroke-48")}),-1.0]])]});
            var Q12;
            Q12=makeQuery(id+"F18.imprint","IMPRINT",FACE,{"disambiguationData":[TD([[makeQuery(id+"F18.imprint","IMPRINT",EDGE,{"derivedFrom":sQuery(id+"F18.wireOp",EDGE,"E161.sketch_text.stroke-102")}),-1.0]])]});
            var Q13;
            Q13=makeQuery(id+"F18.imprint","IMPRINT",FACE,{"disambiguationData":[TD([[makeQuery(id+"F18.imprint","IMPRINT",EDGE,{"derivedFrom":sQuery(id+"F18.wireOp",EDGE,"E97")}),1.0]])]});
            extrude(context, id + "F19", {"entities" : qUnion([Q0, Q1, Q2, Q3, Q4, Q5, Q6, Q7, Q8, Q9, Q10, Q11, Q12, Q13]), "operationType" : NewBodyOperationType.ADD, "depth" : .5 * mm, "offsetDistance" : 25 * mm});
        }
    });
